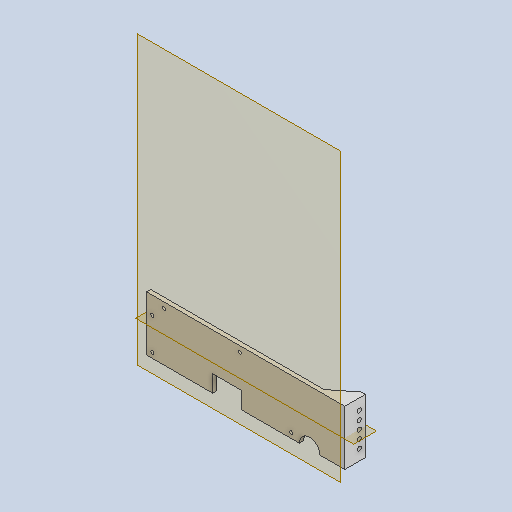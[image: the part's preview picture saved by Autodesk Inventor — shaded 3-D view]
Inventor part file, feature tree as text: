
AUTODESK INVENTOR PART (.ipt)
format: ipt  version: 2022 (Build 260153000, 153)  size: 170,496 bytes
history: native  units: in
note: dims shown in document units (in); Inventor stores cm internally (conversion verified against a paired STEP export)
features: other x6, sketch x6, reference x4, extrude x2, plane x2
ambient origin geometry x8: Origin, YZ Plane, XZ Plane, XY Plane, X Axis, Y Axis, Z Axis, Center Point
bodies: Solid1 (feature_tree)
feature tree (20):
  other  "dilution system bracket.ipt"
  extrude  "Extrusion1"  Depth=0.1969in
  extrude  "Extrusion2"  Depth=0.1969in
  other  "Solid1::dilution system bracket.ipt"
  other  "TaggingFeature1"
  sketch  "Sketch1"  dims[d0=0.3937in d1=0.1969in]
  sketch  "Sketch2"  dims[d2=0.1969in d3=0.1969in]
  sketch  "Sketch3"  dims[d4=0.0in d5=0.0in]
  sketch  "Sketch4"  dims[d6=0.9843in]
  plane  "Work Plane1"
  plane  "Work Plane2"
  sketch  "Sketch5"  dims[d7=0.0in d8=0.0in]
  reference  "Reference1"
  reference  "Reference2"
  reference  "Reference3"
  reference  "Reference4"
  sketch  "Sketch6"
  other  "Linear Rail Assembly.iam"
  other  "Printer Assembly:1"
  other  "Base_v7:1"
